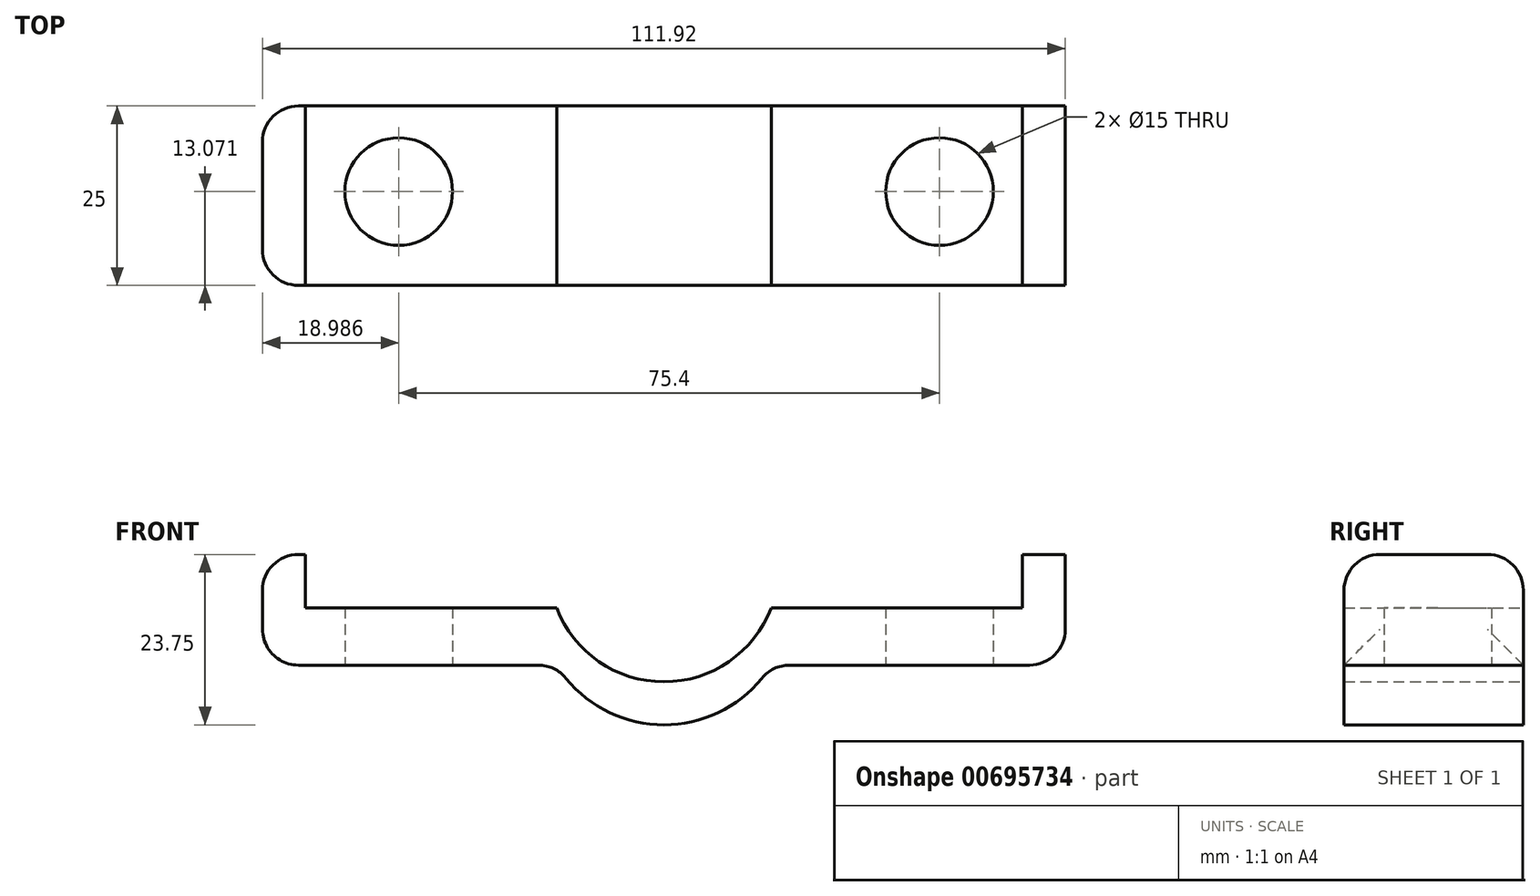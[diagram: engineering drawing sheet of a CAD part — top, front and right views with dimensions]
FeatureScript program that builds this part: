
annotation { "Feature Type Name" : "Feature", "Feature Type Description" : "" }
export const myFeature = defineFeature(function(context is Context, id is Id, definition is map)
    precondition{}
    {
        {
            var Q0;
            Q0=qCreatedBy(makeId("Front.planeOp"),FACE);
            var sketch = newSketch(context, id + "F0", { "sketchPlane" : qUnion([Q0])});
            skLineSegment(sketch, "E0", {"start": v(-42.08, 26.83) * mm, "end": v(-36.08, 26.83) * mm});
            skLineSegment(sketch, "E1", {"start": v(-36.08, 26.83) * mm, "end": v(-36.08, 19.4) * mm});
            skLineSegment(sketch, "E2", {"start": v(-36.08, 19.4) * mm, "end": v(-1.08, 19.4) * mm});
            skLineSegment(sketch, "E3", {"start": v(28.84, 19.4) * mm, "end": v(63.84, 19.4) * mm});
            skLineSegment(sketch, "E4", {"start": v(63.84, 19.4) * mm, "end": v(63.84, 26.83) * mm});
            skLineSegment(sketch, "E5", {"start": v(63.84, 26.83) * mm, "end": v(69.84, 26.83) * mm});
            skLineSegment(sketch, "E6", {"start": v(69.84, 26.83) * mm, "end": v(69.84, 11.4) * mm});
            skLineSegment(sketch, "E7", {"start": v(69.84, 11.4) * mm, "end": v(28.84, 11.4) * mm});
            skLineSegment(sketch, "E8", {"start": v(-1.08, 11.4) * mm, "end": v(-36.08, 11.4) * mm});
            skLineSegment(sketch, "E9", {"start": v(-36.08, 11.4) * mm, "end": v(-42.08, 11.4) * mm});
            skLineSegment(sketch, "E10", {"start": v(-42.08, 11.4) * mm, "end": v(-42.08, 26.83) * mm});
            skArc(sketch, "E11", {"start": v(-1.08, 19.4) * mm, "mid": v(13.88, 9.08) * mm, "end": v(28.84, 19.4) * mm});
            skArc(sketch, "E12", {"start": v(-1.08, 11.4) * mm, "mid": v(13.88, 3.08) * mm, "end": v(28.84, 11.4) * mm});
            skSolve(sketch);
        }
        {
            var Q0;
            Q0 = qSketchRegion(id + "F0", true);
            extrude(context, id + "F1", {"entities" : qUnion([Q0]), "depth" : 25 * mm, "offsetDistance" : 25 * mm});
        }
        {
            var Q0;
            Q0=makeQuery(id+"F1.opExtrude","SWEPT_FACE",FACE,{"disambiguationData":[OSD([sQuery(id+"F0.wireOp",EDGE,"E8"),sQuery(id+"F0.wireOp",EDGE,"E9")])]});
            var sketch = newSketch(context, id + "F2", { "sketchPlane" : qUnion([Q0])});
            skCircle(sketch, "E13", {"center": v(-23.1, 11.93) * mm, "radius": 7.5 * mm});
            skCircle(sketch, "E14", {"center": v(52.3, 11.93) * mm, "radius": 7.5 * mm});
            skSolve(sketch);
        }
        {
            var Q0;
            Q0 = qSketchRegion(id + "F2", true);
            extrude(context, id + "F3", {"entities" : qUnion([Q0]), "operationType" : NewBodyOperationType.REMOVE, "oppositeDirection" : true, "depth" : 25 * mm, "offsetDistance" : 25 * mm});
        }
        {
            var Q0;
            Q0=makeQuery(id+"F1.opExtrude","CAP_EDGE",EDGE,{"disambiguationData":[OSD([sQuery(id+"F0.wireOp",EDGE,"E0")])],"isStart":false});
            var Q1;
            Q1=makeQuery(id+"F1.opExtrude","CAP_EDGE",EDGE,{"disambiguationData":[OSD([sQuery(id+"F0.wireOp",EDGE,"E0")])],"isStart":true});
            var Q2;
            Q2=makeQuery(id+"F1.opExtrude","SWEPT_EDGE",EDGE,{"disambiguationData":[OSD([sQuery(id+"F0.wireOp",EDGE,"E9"),sQuery(id+"F0.wireOp",EDGE,"E10")])]});
            var Q3;
            Q3=makeQuery(id+"F1.opExtrude","SWEPT_EDGE",EDGE,{"disambiguationData":[OSD([sQuery(id+"F0.wireOp",EDGE,"E6"),sQuery(id+"F0.wireOp",EDGE,"E7")])]});
            var Q4;
            Q4=makeQuery(id+"F1.opExtrude","CAP_EDGE",EDGE,{"disambiguationData":[OSD([sQuery(id+"F0.wireOp",EDGE,"E5")])],"isStart":false});
            var Q5;
            Q5=makeQuery(id+"F1.opExtrude","CAP_EDGE",EDGE,{"disambiguationData":[OSD([sQuery(id+"F0.wireOp",EDGE,"E5")])],"isStart":true});
            var Q6;
            Q6=makeQuery(id+"F1.opExtrude","SWEPT_EDGE",EDGE,{"disambiguationData":[OSD([sQuery(id+"F0.wireOp",EDGE,"E8"),sQuery(id+"F0.wireOp",EDGE,"E12")])]});
            var Q7;
            Q7=makeQuery(id+"F1.opExtrude","SWEPT_EDGE",EDGE,{"disambiguationData":[OSD([sQuery(id+"F0.wireOp",EDGE,"E7"),sQuery(id+"F0.wireOp",EDGE,"E12")])]});
            var Q8;
            Q8=makeQuery(id+"F1.opExtrude","SWEPT_EDGE",EDGE,{"disambiguationData":[OSD([sQuery(id+"F0.wireOp",EDGE,"E0"),sQuery(id+"F0.wireOp",EDGE,"E10")])]});
            var Q9;
            Q9=makeQuery(id+"F1.opExtrude","CAP_EDGE",EDGE,{"disambiguationData":[OSD([sQuery(id+"F0.wireOp",EDGE,"E10")])],"isStart":true});
            var Q10;
            Q10=makeQuery(id+"F1.opExtrude","CAP_EDGE",EDGE,{"disambiguationData":[OSD([sQuery(id+"F0.wireOp",EDGE,"E10")])],"isStart":false});
            fillet(context, id + "F4", {"entities" : qUnion([Q0, Q1, Q2, Q3, Q4, Q5, Q6, Q7, Q8, Q9, Q10]), "radius" : 5 * mm, "tangentPropagation" : true, "allowEdgeOverflow" : false});
        }
    });
